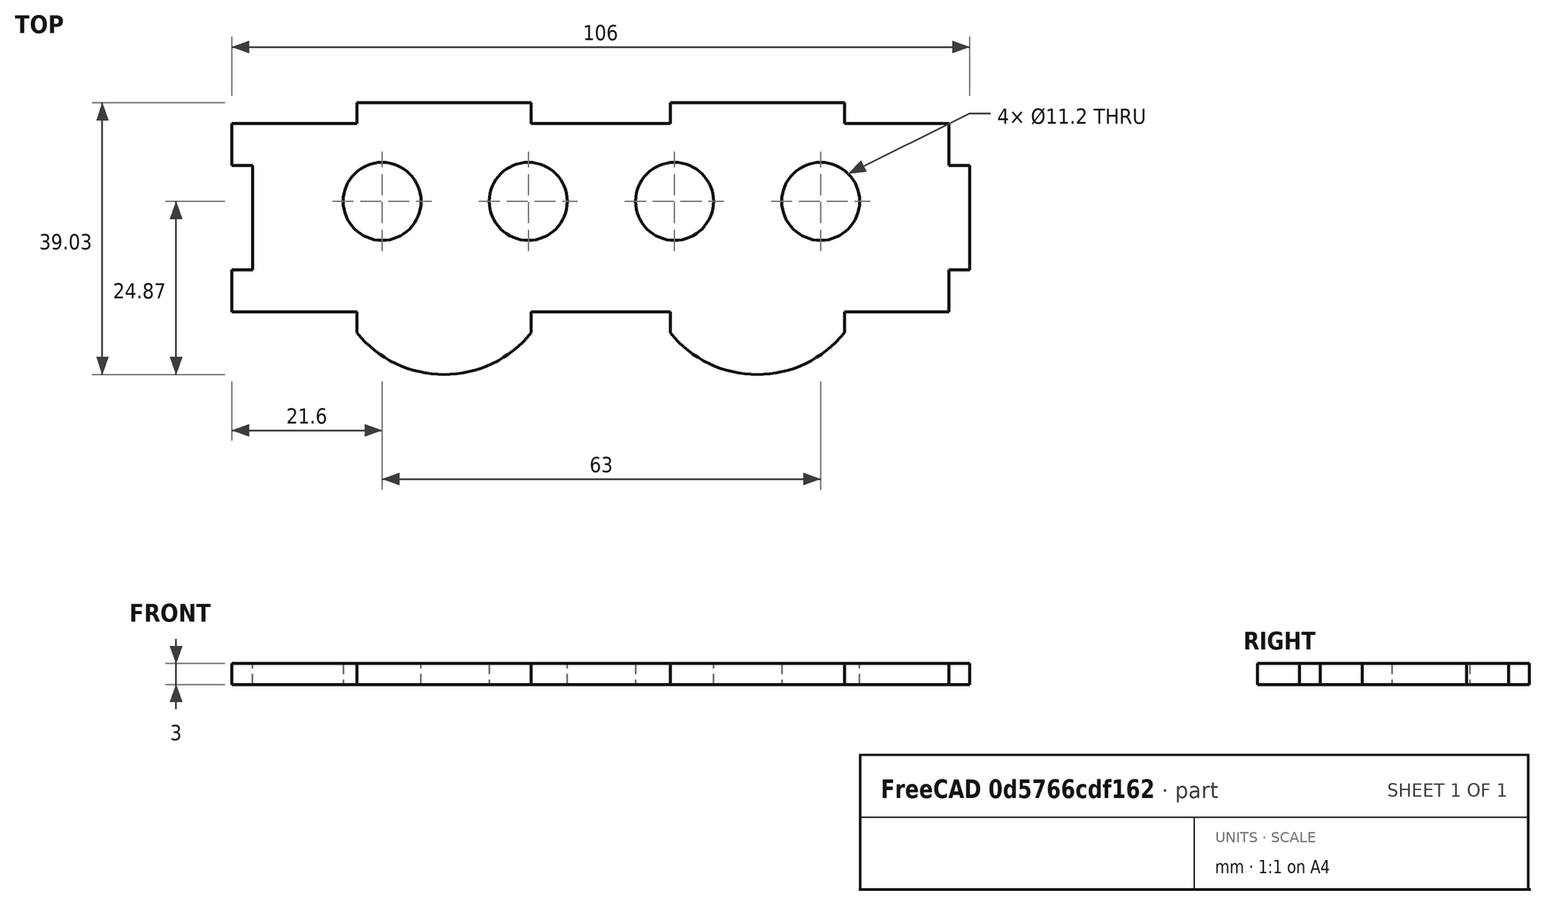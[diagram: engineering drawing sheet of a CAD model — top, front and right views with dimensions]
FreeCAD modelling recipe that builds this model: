
FCSTD DOCUMENT  (FreeCAD 0.19R24267 +99 (Git))
Label: side2
License: All rights reserved
LicenseURL: http://en.wikipedia.org/wiki/All_rights_reserved
objects: App::Part×1, Sketcher::SketchObject×1, Part::Extrusion×1
note: 2 computed .brp shape members not serialized (recipe doc carries the construction recipe); baked Part::Feature solids carry a one-line shape summary decoded from their .brp

FEATURE [App::Part] Part
  Origin = -> Origin
FEATURE [Sketcher::SketchObject] Sketch
  FullyConstrained = false
  sketch-geometry (52):
    g0: LineSegment StartX=0 StartY=0 StartZ=0 EndX=100 EndY=0 EndZ=0
    g1: LineSegment StartX=100 StartY=0 StartZ=0 EndX=100 EndY=1.6 EndZ=0
    g2: LineSegment StartX=100 StartY=1.6 StartZ=0 EndX=0 EndY=1.6 EndZ=0
    g3: LineSegment StartX=0 StartY=1.6 StartZ=0 EndX=0 EndY=0 EndZ=0
    g4: LineSegment StartX=0 StartY=-6.37 StartZ=0 EndX=100 EndY=-6.37 EndZ=0
    g5: LineSegment StartX=100 StartY=-6.37 StartZ=0 EndX=100 EndY=20.66 EndZ=0
    g6: LineSegment StartX=100 StartY=20.66 StartZ=0 EndX=0 EndY=20.66 EndZ=0
    g7: LineSegment StartX=0 StartY=20.66 StartZ=0 EndX=0 EndY=-6.37 EndZ=0
    g8: LineSegment StartX=15 StartY=-6.37 StartZ=0 EndX=40 EndY=-6.37 EndZ=0
    g9: LineSegment StartX=40 StartY=-6.37 StartZ=0 EndX=40 EndY=-9.37 EndZ=0
    g10: LineSegment StartX=40 StartY=-9.37 StartZ=0 EndX=15 EndY=-9.37 EndZ=0
    g11: LineSegment StartX=15 StartY=-9.37 StartZ=0 EndX=15 EndY=-6.37 EndZ=0
    g12: LineSegment StartX=60 StartY=-6.37 StartZ=0 EndX=85 EndY=-6.37 EndZ=0
    g13: LineSegment StartX=85 StartY=-6.37 StartZ=0 EndX=85 EndY=-9.37 EndZ=0
    g14: LineSegment StartX=85 StartY=-9.37 StartZ=0 EndX=60 EndY=-9.37 EndZ=0
    g15: LineSegment StartX=60 StartY=-9.37 StartZ=0 EndX=60 EndY=-6.37 EndZ=0
    g16: LineSegment StartX=15 StartY=20.66 StartZ=0 EndX=40 EndY=20.66 EndZ=0
    g17: LineSegment StartX=40 StartY=20.66 StartZ=0 EndX=40 EndY=23.66 EndZ=0
    g18: LineSegment StartX=40 StartY=23.66 StartZ=0 EndX=15 EndY=23.66 EndZ=0
    g19: LineSegment StartX=15 StartY=23.66 StartZ=0 EndX=15 EndY=20.66 EndZ=0
    g20: LineSegment StartX=60 StartY=20.66 StartZ=0 EndX=85 EndY=20.66 EndZ=0
    g21: LineSegment StartX=85 StartY=20.66 StartZ=0 EndX=85 EndY=23.66 EndZ=0
    g22: LineSegment StartX=85 StartY=23.66 StartZ=0 EndX=60 EndY=23.66 EndZ=0
    g23: LineSegment StartX=60 StartY=23.66 StartZ=0 EndX=60 EndY=20.66 EndZ=0
    g24: LineSegment StartX=100 StartY=14.66 StartZ=0 EndX=103 EndY=14.66 EndZ=0
    g25: LineSegment StartX=103 StartY=14.66 StartZ=0 EndX=103 EndY=-0.34 EndZ=0
    g26: LineSegment StartX=103 StartY=-0.34 StartZ=0 EndX=100 EndY=-0.34 EndZ=0
    g27: LineSegment StartX=100 StartY=-0.34 StartZ=0 EndX=100 EndY=14.66 EndZ=0
    g28: LineSegment StartX=0 StartY=-0.34 StartZ=0 EndX=0 EndY=14.66 EndZ=0
    g29: LineSegment StartX=0 StartY=20.66 StartZ=0 EndX=15 EndY=20.66 EndZ=0
    g30: LineSegment StartX=40 StartY=20.66 StartZ=0 EndX=60 EndY=20.66 EndZ=0
    g31: LineSegment StartX=85 StartY=20.66 StartZ=0 EndX=100 EndY=20.66 EndZ=0
    g32: LineSegment StartX=100 StartY=-0.34 StartZ=0 EndX=100 EndY=-6.37 EndZ=0
    g33: LineSegment StartX=100 StartY=-6.37 StartZ=0 EndX=85 EndY=-6.37 EndZ=0
    g34: LineSegment StartX=60 StartY=-6.37 StartZ=0 EndX=40 EndY=-6.37 EndZ=0
    g35: LineSegment StartX=15 StartY=-6.37 StartZ=0 EndX=0 EndY=-6.37 EndZ=0
    g36: LineSegment StartX=100 StartY=20.66 StartZ=0 EndX=100 EndY=14.66 EndZ=0
    g37: ArcOfCircle CenterX=27.5 CenterY=0.650833 CenterZ=0 NormalX=0 NormalY=0 NormalZ=1 AngleXU=0 Radius=16.0208 StartAngle=3.81735 EndAngle=5.60743
    g38: GeomPoint X=27.5 Y=-15.37 Z=0
    g39: ArcOfCircle CenterX=72.5 CenterY=0.650833 CenterZ=0 NormalX=0 NormalY=0 NormalZ=1 AngleXU=0 Radius=16.0208 StartAngle=3.81735 EndAngle=5.60743
    g40: GeomPoint X=72.5 Y=-15.37 Z=0
    g41: LineSegment StartX=0 StartY=14.66 StartZ=0 EndX=-3 EndY=14.66 EndZ=0
    g42: LineSegment StartX=-3 StartY=-0.34 StartZ=0 EndX=0 EndY=-0.34 EndZ=0
    g43: LineSegment StartX=-3 StartY=-0.34 StartZ=0 EndX=-3 EndY=-6.37 EndZ=0
    g44: LineSegment StartX=-3 StartY=-6.37 StartZ=0 EndX=0 EndY=-6.37 EndZ=0
    g45: LineSegment StartX=-3 StartY=14.66 StartZ=0 EndX=-3 EndY=20.66 EndZ=0
    g46: LineSegment StartX=-3 StartY=20.66 StartZ=0 EndX=0 EndY=20.66 EndZ=0
    g47: LineSegment StartX=0 StartY=14.66 StartZ=0 EndX=0 EndY=-0.34 EndZ=0
    g48: Circle CenterX=18.6 CenterY=9.5 CenterZ=0 NormalX=0 NormalY=0 NormalZ=1 AngleXU=0 Radius=5.6
    g49: Circle CenterX=39.6 CenterY=9.5 CenterZ=0 NormalX=0 NormalY=0 NormalZ=1 AngleXU=0 Radius=5.6
    g50: Circle CenterX=60.6 CenterY=9.5 CenterZ=0 NormalX=0 NormalY=0 NormalZ=1 AngleXU=0 Radius=5.6
    g51: Circle CenterX=81.6 CenterY=9.5 CenterZ=0 NormalX=0 NormalY=0 NormalZ=1 AngleXU=0 Radius=5.6
  constraints (141):
    c: Coincident(g0,g1)
    c: Coincident(g1,g2)
    c: Coincident(g2,g3)
    c: Coincident(g3,g0)
    c: Horizontal(g0)
    c: Horizontal(g2)
    c: Vertical(g1)
    c: Vertical(g3)
    c: Coincident(g0,g-1)
    c: DistanceX(g2,g2) = 100
    c: DistanceY(g3,g3) = 1.6
    c: Coincident(g4,g5)
    c: Coincident(g5,g6)
    c: Coincident(g6,g7)
    c: Coincident(g7,g4)
    c: Horizontal(g4)
    c: Horizontal(g6)
    c: Vertical(g5)
    c: Vertical(g7)
    c: PointOnObject(g4,g-2)
    c: Equal(g6,g2)
    c: DistanceY(g2,g6) = 19.06
    c: DistanceY(g4,g-1) = 6.37
    c: Coincident(g8,g9)
    c: Coincident(g9,g10)
    c: Coincident(g10,g11)
    c: Coincident(g11,g8)
    c: Horizontal(g8)
    c: Horizontal(g10)
    c: Vertical(g9)
    c: Vertical(g11)
    c: PointOnObject(g8,g4)
    c: Coincident(g12,g13)
    c: Coincident(g13,g14)
    c: Coincident(g14,g15)
    c: Coincident(g15,g12)
    c: Horizontal(g12)
    c: Horizontal(g14)
    c: Vertical(g13)
    c: Vertical(g15)
    c: PointOnObject(g12,g4)
    c: Coincident(g16,g17)
    c: Coincident(g17,g18)
    c: Coincident(g18,g19)
    c: Coincident(g19,g16)
    c: Horizontal(g16)
    c: Horizontal(g18)
    c: Vertical(g17)
    c: Vertical(g19)
    c: PointOnObject(g16,g6)
    c: Coincident(g20,g21)
    c: Coincident(g21,g22)
    c: Coincident(g22,g23)
    c: Coincident(g23,g20)
    c: Horizontal(g20)
    c: Horizontal(g22)
    c: Vertical(g21)
    c: Vertical(g23)
    c: PointOnObject(g20,g6)
    c: Coincident(g24,g25)
    c: Coincident(g25,g26)
    c: Coincident(g26,g27)
    c: Coincident(g27,g24)
    c: Horizontal(g24)
    c: Horizontal(g26)
    c: Vertical(g25)
    c: Vertical(g27)
    c: PointOnObject(g24,g5)
    c: Vertical(g28)
    c: PointOnObject(g28,g7)
    c: Equal(g18,g22)
    c: Equal(g14,g10)
    c: DistanceX(g18,g18) = 25
    c: Equal(g11,g15)
    c: Equal(g15,g23)
    c: Equal(g23,g24)
    c: DistanceY(g23,g23) = 3
    c: DistanceX(g6,g18) = 15
    c: DistanceX(g21,g5) = 15
    c: DistanceX(g13,g4) = 15
    c: DistanceX(g4,g10) = 15
    c: Equal(g14,g22)
    c: DistanceY(g25,g25) = 15
    c: DistanceY(g24,g5) = 6
    c: Coincident(g29,g16)
    c: Coincident(g30,g16)
    c: Coincident(g30,g20)
    c: Coincident(g31,g20)
    c: Coincident(g31,g5)
    c: Coincident(g32,g26)
    c: Coincident(g32,g4)
    c: Coincident(g33,g32)
    c: Coincident(g33,g12)
    c: Coincident(g34,g12)
    c: Coincident(g34,g8)
    c: Coincident(g35,g8)
    c: Coincident(g35,g4)
    c: Coincident(g36,g31)
    c: Coincident(g36,g24)
    c: Coincident(g37,g9)
    c: Coincident(g37,g10)
    c: PointOnObject(g38,g37)
    c: DistanceY(g38,g9) = 6
    c: DistanceX(g38,g9) = 12.5
    c: Coincident(g39,g14)
    c: Coincident(g39,g13)
    c: PointOnObject(g40,g39)
    c: DistanceX(g40,g13) = 12.5
    c: DistanceY(g40,g13) = 6
    c: Coincident(g41,g28)
    c: Horizontal(g41)
    c: PointOnObject(g42,g7)
    c: Horizontal(g42)
    c: DistanceY(g42,g41) = 15
    c: DistanceX(g41,g41) = 3
    c: Horizontal(g41,g24)
    c: Vertical(g43)
    c: Coincident(g44,g43)
    c: Coincident(g44,g35)
    c: Horizontal(g44)
    c: Coincident(g45,g41)
    c: Vertical(g45)
    c: Coincident(g46,g29)
    c: Horizontal(g46)
    c: Horizontal(g29,g19)
    c: Coincident(g47,g41)
    c: Coincident(g47,g42)
    c: DistanceY(g45,g45) = 6
    c: Equal(g43,g32)
    c: Equal(g48,g49)
    c: Equal(g49,g50)
    c: Equal(g50,g51)
    c: Radius(g50) = 5.6
    c: Horizontal(g48,g49)
    c: Horizontal(g49,g50)
    c: Horizontal(g50,g51)
    c: DistanceX(g48,g49) = 21
    c: DistanceX(g49,g50) = 21
    c: DistanceX(g50,g51) = 21
    c: DistanceX(g51,g1) = 18.4
    c: DistanceY(g2,g49) = 7.9
FEATURE [Part::Extrusion] Extrude
  Base = -> Sketch
  Dir = (0,0,1)
  DirMode = 2
  FaceMakerClass = Part::FaceMakerBullseye
  LengthFwd = 3
  LengthRev = 0
  Solid = true
  Symmetric = false
